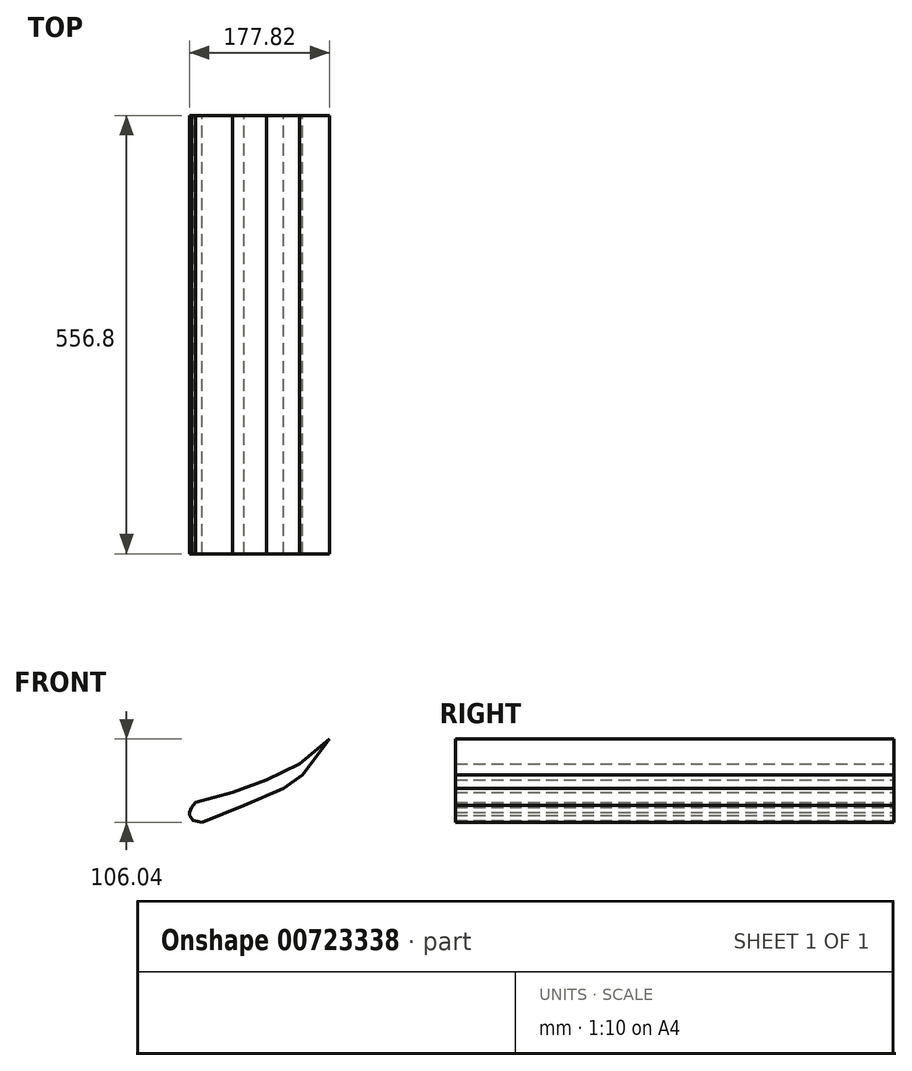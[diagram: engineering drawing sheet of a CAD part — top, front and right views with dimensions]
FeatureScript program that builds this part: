
annotation { "Feature Type Name" : "Feature", "Feature Type Description" : "" }
export const myFeature = defineFeature(function(context is Context, id is Id, definition is map)
    precondition{}
    {
        {
            var Q0;
            Q0=qCreatedBy(makeId("Front.planeOp"),FACE);
            var sketch = newSketch(context, id + "F0", { "sketchPlane" : qUnion([Q0])});
            skLineSegment(sketch, "E0", {"start": v(96.76, -49.14) * mm, "end": v(143.66, -36.66) * mm});
            skLineSegment(sketch, "E1", {"start": v(143.66, -36.66) * mm, "end": v(186.86, -20.33) * mm});
            skLineSegment(sketch, "E2", {"start": v(186.86, -20.33) * mm, "end": v(229.09, 0) * mm});
            skLineSegment(sketch, "E3", {"start": v(229.09, 0) * mm, "end": v(266.92, 31.57) * mm});
            skLineSegment(sketch, "E4", {"start": v(266.92, 31.57) * mm, "end": v(232.83, -14) * mm});
            skLineSegment(sketch, "E5", {"start": v(232.83, -14) * mm, "end": v(208.67, -31.62) * mm});
            skLineSegment(sketch, "E6", {"start": v(208.67, -31.62) * mm, "end": v(158.46, -53.09) * mm});
            skLineSegment(sketch, "E7", {"start": v(158.46, -53.09) * mm, "end": v(105.2, -74.47) * mm});
            skLineSegment(sketch, "E8", {"start": v(105.2, -74.47) * mm, "end": v(93.28, -71.85) * mm});
            skLineSegment(sketch, "E9", {"start": v(93.28, -71.85) * mm, "end": v(89.1, -65.87) * mm});
            skLineSegment(sketch, "E10", {"start": v(89.1, -65.87) * mm, "end": v(89.1, -62.15) * mm});
            skLineSegment(sketch, "E11", {"start": v(89.1, -62.15) * mm, "end": v(91.55, -55.53) * mm});
            skLineSegment(sketch, "E12", {"start": v(91.55, -55.53) * mm, "end": v(96.76, -49.14) * mm});
            skSolve(sketch);
        }
        {
            var Q0;
            Q0=makeQuery(id+"F0.imprint","IMPRINT",FACE,{"disambiguationData":[TD([[makeQuery(id+"F0.imprint","IMPRINT",EDGE,{"derivedFrom":sQuery(id+"F0.wireOp",EDGE,"E0")}),-1.0]])]});
            var sketch = newSketch(context, id + "F1", { "sketchPlane" : qUnion([Q0])});
            skSolve(sketch);
        }
        {
            var Q0;
            Q0=makeQuery(id+"F1.imprint","IMPRINT",FACE,{"disambiguationData":[TD([[makeQuery(id+"F1.imprint","IMPRINT",EDGE,{"derivedFrom":makeQuery(id+"F0.imprint","IMPRINT",EDGE,{"derivedFrom":sQuery(id+"F0.wireOp",EDGE,"E0")})}),-1.0]])]});
            extrude(context, id + "F2", {"entities" : qUnion([Q0]), "depth" : 556.8 * mm, "offsetDistance" : 25.4 * mm});
        }
    });
